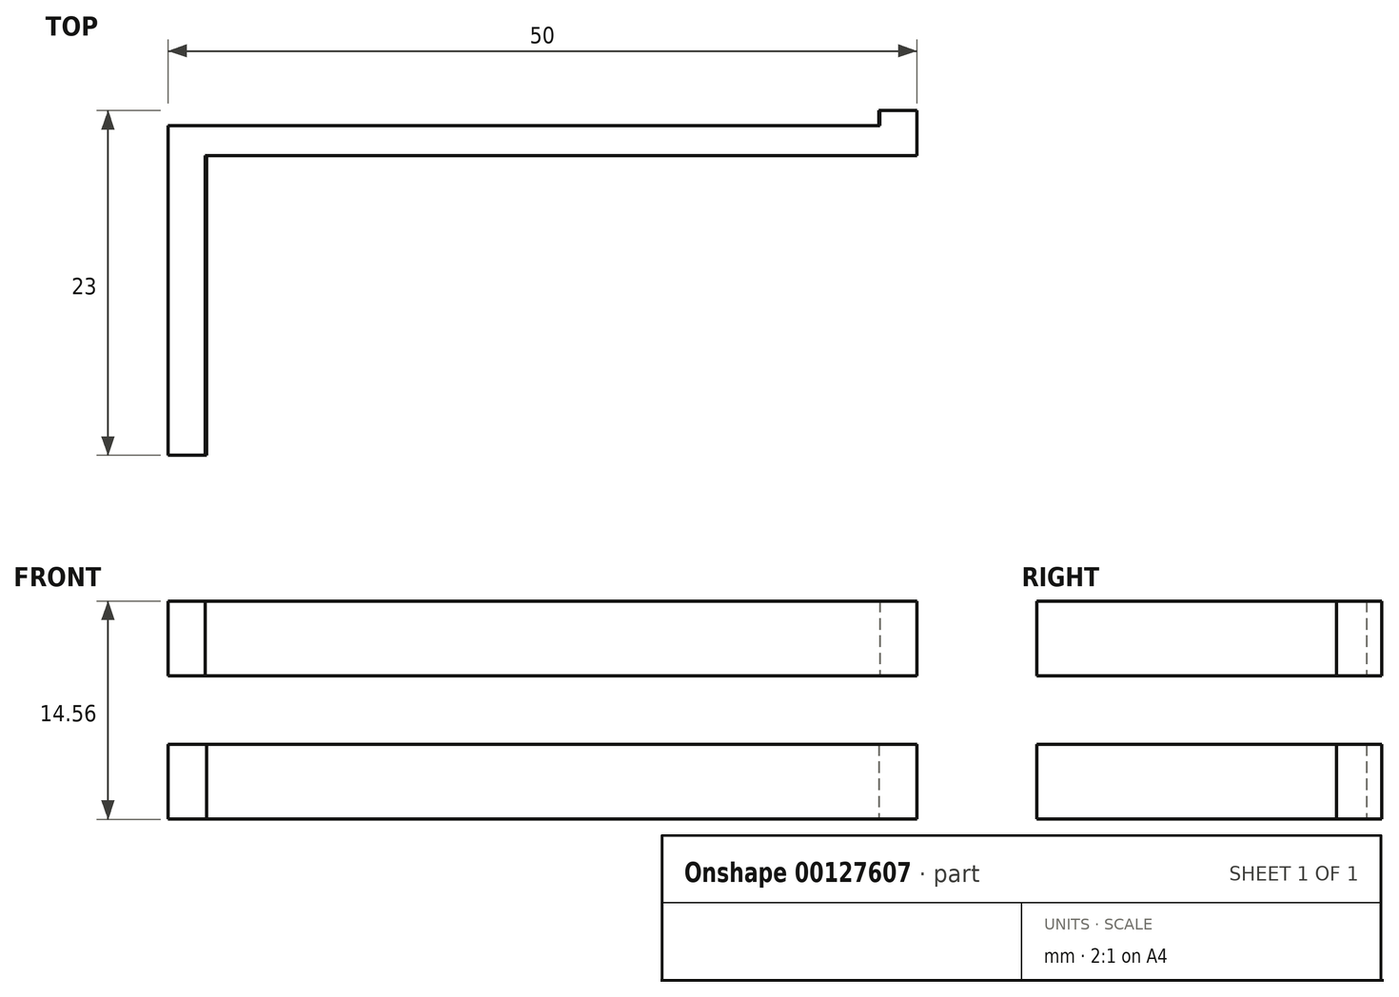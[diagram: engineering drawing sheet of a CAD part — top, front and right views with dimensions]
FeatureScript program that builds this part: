
annotation { "Feature Type Name" : "Feature", "Feature Type Description" : "" }
export const myFeature = defineFeature(function(context is Context, id is Id, definition is map)
    precondition{}
    {
        {
            var Q0;
            Q0=qCreatedBy(makeId("Front.planeOp"),FACE);
            var sketch = newSketch(context, id + "F0", { "sketchPlane" : qUnion([Q0])});
            skLineSegment(sketch, "E0.bottom", {"start": v(-50, 7.57) * mm, "end": v(0, 7.57) * mm});
            skLineSegment(sketch, "E0.top", {"start": v(-50, 2.57) * mm, "end": v(0, 2.57) * mm});
            skLineSegment(sketch, "E0.left", {"start": v(-50, 7.57) * mm, "end": v(-50, 2.57) * mm});
            skLineSegment(sketch, "E0.right", {"start": v(0, 7.57) * mm, "end": v(0, 2.57) * mm});
            skLineSegment(sketch, "E1.bottom", {"start": v(-50, -1.99) * mm, "end": v(0, -1.99) * mm});
            skLineSegment(sketch, "E1.top", {"start": v(-50, -6.99) * mm, "end": v(0, -6.99) * mm});
            skLineSegment(sketch, "E1.left", {"start": v(-50, -1.99) * mm, "end": v(-50, -6.99) * mm});
            skLineSegment(sketch, "E1.right", {"start": v(0, -1.99) * mm, "end": v(0, -6.99) * mm});
            skSolve(sketch);
        }
        {
            var Q0;
            Q0 = qSketchRegion(id + "F0", true);
            extrude(context, id + "F1", {"entities" : qUnion([Q0]), "depth" : 2 * mm});
        }
        {
            var Q0;
            Q0=makeQuery(id+"F1.opExtrude","CAP_FACE",FACE,{"disambiguationData":[OSD([sQuery(id+"F0.wireOp",EDGE,"E0.bottom"),sQuery(id+"F0.wireOp",EDGE,"E0.top"),sQuery(id+"F0.wireOp",EDGE,"E0.left"),sQuery(id+"F0.wireOp",EDGE,"E0.right")])],"isStart":false});
            var sketch = newSketch(context, id + "F2", { "sketchPlane" : qUnion([Q0])});
            skLineSegment(sketch, "E2.bottom", {"start": v(-50, 2.57) * mm, "end": v(-47.5, 2.57) * mm});
            skLineSegment(sketch, "E2.top", {"start": v(-50, 7.57) * mm, "end": v(-47.5, 7.57) * mm});
            skLineSegment(sketch, "E2.left", {"start": v(-50, 2.57) * mm, "end": v(-50, 7.57) * mm});
            skLineSegment(sketch, "E2.right", {"start": v(-47.5, 2.57) * mm, "end": v(-47.5, 7.57) * mm});
            skSolve(sketch);
        }
        {
            var Q0;
            Q0 = qSketchRegion(id + "F2", true);
            extrude(context, id + "F3", {"entities" : qUnion([Q0]), "operationType" : NewBodyOperationType.ADD, "depth" : 20 * mm});
        }
        {
            var Q0;
            Q0=makeQuery(id+"F1.opExtrude","CAP_FACE",FACE,{"disambiguationData":[OSD([sQuery(id+"F0.wireOp",EDGE,"E1.bottom"),sQuery(id+"F0.wireOp",EDGE,"E1.top"),sQuery(id+"F0.wireOp",EDGE,"E1.left"),sQuery(id+"F0.wireOp",EDGE,"E1.right")])],"isStart":false});
            var sketch = newSketch(context, id + "F4", { "sketchPlane" : qUnion([Q0])});
            skLineSegment(sketch, "E3.bottom", {"start": v(-50, -1.99) * mm, "end": v(-47.43, -1.99) * mm});
            skLineSegment(sketch, "E3.top", {"start": v(-50, -6.99) * mm, "end": v(-47.43, -6.99) * mm});
            skLineSegment(sketch, "E3.left", {"start": v(-50, -1.99) * mm, "end": v(-50, -6.99) * mm});
            skLineSegment(sketch, "E3.right", {"start": v(-47.43, -1.99) * mm, "end": v(-47.43, -6.99) * mm});
            skSolve(sketch);
        }
        {
            var Q0;
            Q0 = qSketchRegion(id + "F4", true);
            extrude(context, id + "F5", {"entities" : qUnion([Q0]), "operationType" : NewBodyOperationType.ADD, "depth" : 20 * mm});
        }
        {
            var Q0;
            Q0=makeQuery(id+"F1.opExtrude","CAP_FACE",FACE,{"disambiguationData":[OSD([sQuery(id+"F0.wireOp",EDGE,"E0.bottom"),sQuery(id+"F0.wireOp",EDGE,"E0.top"),sQuery(id+"F0.wireOp",EDGE,"E0.left"),sQuery(id+"F0.wireOp",EDGE,"E0.right")])],"isStart":false});
            var sketch = newSketch(context, id + "F6", { "sketchPlane" : qUnion([Q0])});
            skLineSegment(sketch, "E4.bottom", {"start": v(0, 7.57) * mm, "end": v(-2.5, 7.57) * mm});
            skLineSegment(sketch, "E4.top", {"start": v(0, 2.57) * mm, "end": v(-2.5, 2.57) * mm});
            skLineSegment(sketch, "E4.left", {"start": v(0, 7.57) * mm, "end": v(0, 2.57) * mm});
            skLineSegment(sketch, "E4.right", {"start": v(-2.5, 7.57) * mm, "end": v(-2.5, 2.57) * mm});
            skSolve(sketch);
        }
        {
            var Q0;
            Q0 = qSketchRegion(id + "F6", true);
            extrude(context, id + "F7", {"entities" : qUnion([Q0]), "operationType" : NewBodyOperationType.ADD, "oppositeDirection" : true, "depth" : 3 * mm});
        }
        {
            var Q0;
            Q0=makeQuery(id+"F1.opExtrude","CAP_FACE",FACE,{"disambiguationData":[OSD([sQuery(id+"F0.wireOp",EDGE,"E1.bottom"),sQuery(id+"F0.wireOp",EDGE,"E1.top"),sQuery(id+"F0.wireOp",EDGE,"E1.left"),sQuery(id+"F0.wireOp",EDGE,"E1.right")])],"isStart":false});
            var sketch = newSketch(context, id + "F8", { "sketchPlane" : qUnion([Q0])});
            skLineSegment(sketch, "E5.bottom", {"start": v(0, -1.99) * mm, "end": v(-2.55, -1.99) * mm});
            skLineSegment(sketch, "E5.top", {"start": v(0, -6.99) * mm, "end": v(-2.55, -6.99) * mm});
            skLineSegment(sketch, "E5.left", {"start": v(0, -1.99) * mm, "end": v(0, -6.99) * mm});
            skLineSegment(sketch, "E5.right", {"start": v(-2.55, -1.99) * mm, "end": v(-2.55, -6.99) * mm});
            skSolve(sketch);
        }
        {
            var Q0;
            Q0 = qSketchRegion(id + "F8", true);
            extrude(context, id + "F9", {"entities" : qUnion([Q0]), "operationType" : NewBodyOperationType.ADD, "oppositeDirection" : true, "depth" : 3 * mm});
        }
    });
